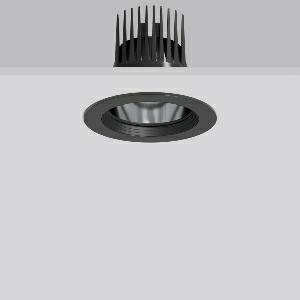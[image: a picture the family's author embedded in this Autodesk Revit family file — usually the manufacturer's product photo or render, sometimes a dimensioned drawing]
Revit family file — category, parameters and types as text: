
# Revit family: heledon_maxi_e_901763_003_2_76_a624
name_source: partatom
category: Lighting Fixtures
units: mm (PartAtom-declared; Revit-internal decimal feet)

## family parameters
Cut with Voids When Loaded = No
Host = Face
Light Source = No
Part Type = Normal
Room Calculation Point = No
Round Connector Dimension = Use Diameter
Shared = No

## types (1)
- HELEDON maxi E (1 x LED Modul 927, 4000 lm, 2700)
    Apparent Load = 35 VA
    Approval mark = CE
    CIE Flux Codes = 100 100 100 100 100
    Color Rendering = 92
    Color Temperature = 2700
    Default Elevation = 1800 mm
    Description = Series: HELEDON maxi
Round recessed downlight. Housing: die-cast aluminium, powder-coated. Black plastic ring and recessed LED to prevent glare from the side. Optical assembly with reflector made of MIRO-Silver with 98% total light reflection for outstanding efficiency - can be changed without tools. Best colour rendering index Ra>90. Suitable for Recessed ceiling mounting. Installation without tools thanks to spring fastening system. Including separate LED converter with connecting cable 600 mm.High quality converter without flickering and stroboscopic effect. Through-wiring box (5 pole) available as accessory. The following accessories can be mounted without use of tools: interchangeable lenses, decorative glasses, honeycomb louvre, clear and frosted diffusers, white interchangeable plastic ring. 
Colour: deep black, matt (RAL 9005)
Diameter: 162 mm
Height: 3 mm
Cut-out diameter: 152 mm
Recess height: 200 mm
Luminaire: recess height: 135 mm
Lamp: LED
Socket: without socket
Colour temperature: 2700K
Colour rendering index (CRI): 92
System power: 35 W
Rated luminous flux: 4000 lm
Luminous efficiency: 114 lm/W
Control gear: Converter, dimmable, DALI
Protection class: II
Type of protection: IP 20
    Height = 0 mm  [stored 0 ft]
    Lamp = 1 x LED Modul 927
    Lamp Light Flux = 4000 lm
    Lamp count = 1
    Length = 162 mm
    Lifetime = 50000 h
    Luminous efficacy = 114 lm/W
    Manufacturer = RZB
    ModVariant = No
    Model = 901763.003.2.76
    Mounting Place = Ceiling
    Mounting Type = Recessed
    Number of Poles = 1
    OnlyDefault = Yes
    Power Factor = 1
    Product Name = HELEDON maxi E
    Product group = Recessed downlights
    ProductGroupID = 402
    Protection Class = Protection class II
    Protection Degree = IP 20
    RLX_Detail_Level = 1
    RLX_Emergency_Light_Flux = 0 lm
    RLX_Emergency_Type = 0
    RLX_Emergency_Type_DB = No
    RlxData = <blob elided: 122797 chars, md5=557b667b>
    Socket = socket
    Standby Power = 0 W
    System Light Flux = 4000 lm
    System Power = 35 W
    Type Comments = Product without accessories
    Type Image = 901662.003.jpg
    URL = http://relux.com
    VarID = ---
    Voltage = 230 V
    Voltage Range = 220-240 V
    Weight = 0.00 kg
    Width = 0 mm  [stored 0 ft]

note: [stored X ft] marks values corroborated as IEEE doubles in the binary element streams (Revit-internal decimal feet)

## geometry (parser evidence)
native form markers: Blend x4, Sweep x13
no freeform markers — native parametric forms only
